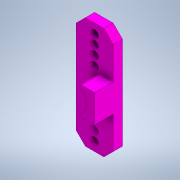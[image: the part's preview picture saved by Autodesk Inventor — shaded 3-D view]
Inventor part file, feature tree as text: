
AUTODESK INVENTOR PART (.ipt)
format: ipt  version: 2020 (Build 240168000, 168)  size: 160,768 bytes
history: native  units: in
note: dims shown in document units (in); Inventor stores cm internally (conversion verified against a paired STEP export)
features: extrude x3, sketch x3, other x3, reference x2, fillet x1, chamfer x1
ambient origin geometry x8: Origin, YZ Plane, XZ Plane, XY Plane, X Axis, Y Axis, Z Axis, Center Point
bodies: Solid1 (feature_tree)
feature tree (13):
  extrude  "Extrusion1"  Depth=1.0in
  extrude  "Extrusion2"  Depth=0.5in
  extrude  "Extrusion3"  Depth=0.25in
  fillet  "Fillet1"  Radius=0.25in
  chamfer  "Chamfer1"  Distance=0.3937in
  sketch  "Sketch1"  dims[d0=3.0in d1=1.0in]
  reference  "Reference1"
  reference  "Reference2"
  sketch  "Sketch2"  dims[d2=0.25in d3=0.0in d4=0.5in]
  sketch  "Sketch3"  dims[d5=0.25in d6=0.2031in d7=1.5748in d9=0.25in d10=0.3937in d12=1.0in d14=0.7874in d16=1.75in d17=0.3937in d19=1.0in d21=0.0in d22=0.0in d23=0.6in d24=1.125in d25=0.75in d26=0.5in d27=0.0in d28=0.04in d29=0.25in d30=0.125in d31=45.0deg]
  other  "<userpath>\Documents\FRC\2020\IntakeShooter\IntakeExtensionBar.iam"
  other  "IntakeExtensionBar.iam"
  other  "1x1x18:1"
